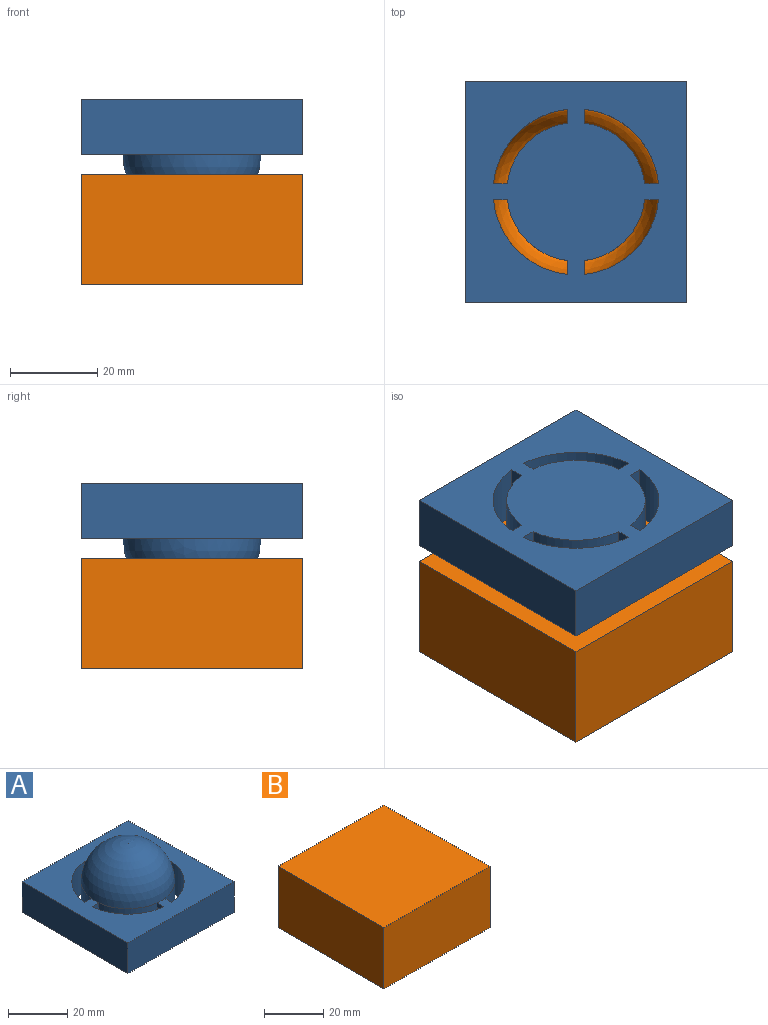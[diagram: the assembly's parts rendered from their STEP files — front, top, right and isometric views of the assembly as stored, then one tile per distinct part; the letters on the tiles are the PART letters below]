
ASSEMBLY  parts=2 mates=2
PART A: 23 faces, bbox 50.8x50.8x28.6 mm
  f0: plane 50.8x50.8mm, normal (0,0,1), area 1487.3mm2, adj f2,f3,f4,f5,f6,f8,f9,f10
  f1: plane 50.8x50.8mm, normal (0,0,-1), area 2279mm2, adj f2,f3,f4,f5,f7,f8,f9,f10
  f2: plane 50.8x12.7mm, normal (0,-1,0), area 645.2mm2, adj f0,f1,f3,f5
  f3: plane 50.8x12.7mm, normal (1,0,0), area 645.2mm2, adj f0,f1,f2,f4
  f4: plane 50.8x12.7mm, normal (0,1,0), area 645.2mm2, adj f0,f1,f3,f5
  f5: plane 50.8x12.7mm, normal (-1,0,0), area 645.2mm2, adj f0,f1,f2,f4
  f6: sphere r=15.88mm, area 1583.5mm2, adj f0,f7,f11,f17,f19
  f7: cylinder r=15.88mm len=13.95mm, axis (0,0,-1), area 269.9mm2, adj f1,f6,f8,f10
  f8: plane 12.7x3.19mm, normal (-1,0,0), area 40.6mm2, adj f0,f1,f7,f9
  f9: cylinder r=19.05mm len=17.15mm, axis (0,0,-1), area 333.3mm2, adj f0,f1,f8,f10
  f10: plane 12.7x3.19mm, normal (0,-1,0), area 40.5mm2, adj f0,f1,f7,f9
  f11: cylinder r=15.88mm len=13.95mm, axis (0,0,-1), area 269.9mm2, adj f1,f6,f12,f14
  f12: plane 12.7x3.19mm, normal (1,0,0), area 40.6mm2, adj f0,f1,f11,f13
  f13: cylinder r=19.05mm len=17.15mm, axis (0,0,-1), area 333.3mm2, adj f0,f1,f12,f14
  f14: plane 12.7x3.19mm, normal (0,1,0), area 40.5mm2, adj f0,f1,f11,f13
  f15: cylinder r=19.05mm len=17.15mm, axis (0,0,-1), area 333.3mm2, adj f0,f1,f16,f18
  f16: plane 12.7x3.19mm, normal (-1,0,0), area 40.6mm2, adj f0,f1,f15,f17
  f17: cylinder r=15.88mm len=13.95mm, axis (0,0,-1), area 269.9mm2, adj f1,f6,f16,f18
  f18: plane 12.7x3.19mm, normal (0,1,0), area 40.5mm2, adj f0,f1,f15,f17
  f19: cylinder r=15.88mm len=13.95mm, axis (0,0,-1), area 269.9mm2, adj f1,f6,f20,f22
  f20: plane 12.7x3.19mm, normal (0,-1,0), area 40.5mm2, adj f0,f1,f19,f21
  f21: cylinder r=19.05mm len=17.15mm, axis (0,0,-1), area 333.3mm2, adj f0,f1,f20,f22
  f22: plane 12.7x3.19mm, normal (1,0,0), area 40.6mm2, adj f0,f1,f19,f21
PART B: 7 faces, bbox 50.8x50.8x25.4 mm
  f0: plane 50.8x25.4mm, normal (0,-1,0), area 1290.3mm2, adj f1,f3,f4,f5
  f1: plane 50.8x25.4mm, normal (1,0,0), area 1290.3mm2, adj f0,f2,f4,f5
  f2: plane 50.8x25.4mm, normal (0,1,0), area 1290.3mm2, adj f1,f3,f4,f5
  f3: plane 50.8x25.4mm, normal (-1,0,0), area 1290.3mm2, adj f0,f2,f4,f5
  f4: plane 50.8x50.8mm, normal (0,0,1), area 2580.6mm2, adj f0,f1,f2,f3
  f5: plane 50.8x50.8mm, normal (0,0,-1), area 1440.5mm2, adj f0,f1,f2,f3,f6
  f6: sphere r=19.05mm, area 2280.2mm2, adj f5
PLACE A rot(axis=(0,1,0),180deg) t=(-20.88,-14.38,26.66)mm
PLACE B rot(axis=(0,1,0),180deg) t=(-20.88,-14.38,9.49)mm fixed
MATE planar B.f2 <-> A.f4  axis (0,1,0) through (-20.88,11.02,-3.21)mm
MATE planar B.f1 <-> A.f3  axis (-1,0,0) through (-46.28,-14.38,-3.21)mm
